# Revit family: ShowerHead-RainLshowerhead-Vitra-ShowerSystems-A45708
name_source: partatom
category: Plumbing Fixtures
revit_build: Autodesk Revit 2017 (Build: 20160225_1515(x64)
units: mm (PartAtom-declared; Revit-internal decimal feet)

## family parameters
Always vertical = No
Cut with Voids When Loaded = No
OmniClass Number = 23.45.00.00
OmniClass Title = Sanitary, Laundry, and Cleaning Equipment
Part Type = Normal
Room Calculation Point = No
Round Connector Dimension = Use Diameter
Shared = Yes
Work Plane-Based = Yes

## types (4) — shared parameters
BIMobject category = Showers
Brand = Vitra
CW Connection = Yes
Coating Material = Chrome
Color = Chrome
Connection Diameter (mm) = 15 mm  [stored 0.0492126 ft]
Default Elevation = 1800 mm  [stored 5.90551 ft]
Description = Faucets&Shower systems&Accessories
HW Connection = Yes
Hot Water Supply (max.) = 80 °C
Hot Water temperature, factory set to = 38 °C
IFC Classification = Sanitary Terminal
Manufacturer = Vitra
Manufacturer name = Vitra
Masterformat 2014 Code = 22 41 23
Masterformat 2014 Description = Residential Showers
Min. flow pressure of = 0.5 bar
Mounting type = Pipe Connect
Nominal Depth (mm) = 220 mm
Nominal Height (mm) = 55 mm  [stored 0.180446 ft]
Nominal Width (mm) = 220 mm
Number Of Connections = 1
OmniClass Code = 23-31 17 19
OmniClass Description = Shower Head Fixtures
Product certification = https://www.vitraglobal.com
Product family = Shower Systems
Product group = Overhead showers
Product url = https://www.vitraglobal.com
Range of Hot Water Supply = 5 - 65 °C
Range of flow pressure = 0.5-10 bar (Recommended 3-5 Bars)
Test Pressure = 16 bar
URL = https://vitraglobal.com
Uniclass 1.4 Code = L7214
Uniclass 1.4 Description = Showers
Uniclass 2.0 Code = PR-35-06-81
Uniclass 2.0 Description = Shower Heads
Uniclass 2015 Code = Pr_40_20_87_76
Uniclass 2015 Name = Shower heads
Uniformat II Code = D2010
Uniformat II Description = Plumbing Fixtures
Vent Connection = No
Warranty Period (Year) = 5
Waste Connection = No

## per-type parameters (varying)
| type | Article No. (default) | Model | Product SKU |
| ShowerHead-Vitra-ShowerSystems-A45708STA | A45708STA | A45708STA | A45708STA |
| ShowerHead-Vitra-ShowerSystems-A45708EXPS | A45708EXPS | A45708EXPS | A45708EXPS |
| ShowerHead-Vitra-ShowerSystems-A45708WSA | A45708WSA | A45708WSA | A45708WSA |
| ShowerHead-Vitra-ShowerSystems-A45708 | A45708 | A45708 | A45708 |

note: [stored X ft] marks values corroborated as IEEE doubles in the binary element streams (Revit-internal decimal feet)

## geometry (parser evidence)
native form markers: Sweep x2
no freeform markers — native parametric forms only
